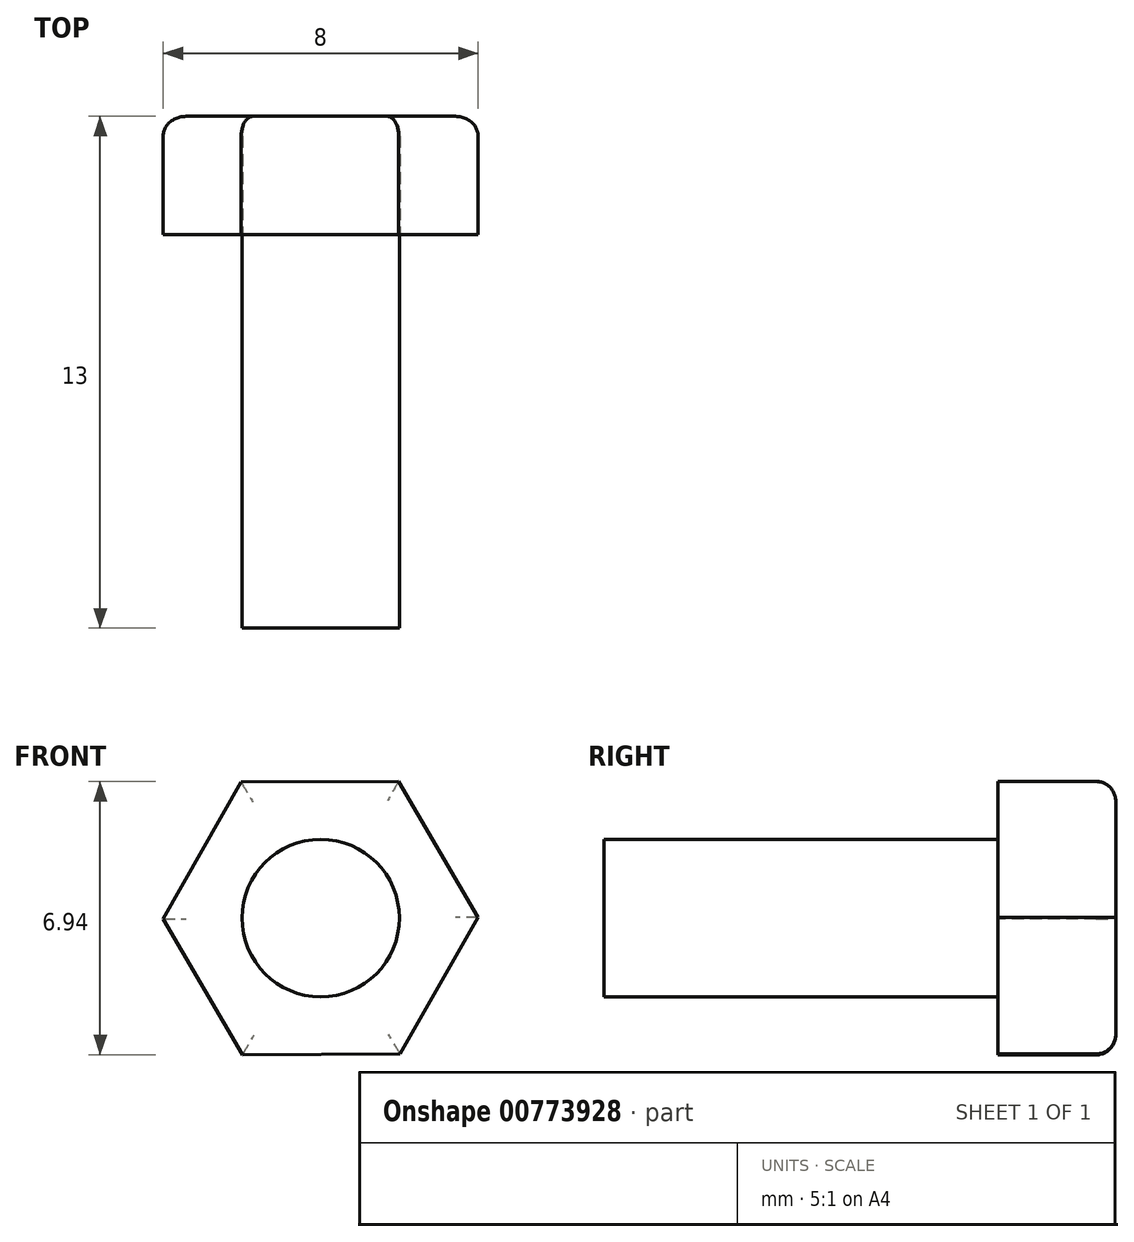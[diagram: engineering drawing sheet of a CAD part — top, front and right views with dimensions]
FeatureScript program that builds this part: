
annotation { "Feature Type Name" : "Feature", "Feature Type Description" : "" }
export const myFeature = defineFeature(function(context is Context, id is Id, definition is map)
    precondition{}
    {
        {
            var Q0;
            Q0=qCreatedBy(makeId("Front.planeOp"),FACE);
            var sketch = newSketch(context, id + "F0", { "sketchPlane" : qUnion([Q0])});
            skCircle(sketch, "E0", {"center": v(0, 0) * mm, "radius": 2 * mm});
            skSolve(sketch);
        }
        {
            var Q0;
            Q0 = qSketchRegion(id + "F0", true);
            extrude(context, id + "F1", {"entities" : qUnion([Q0]), "oppositeDirection" : true, "depth" : 10 * mm, "offsetDistance" : 25 * mm});
        }
        {
            var Q0;
            Q0=makeQuery(id+"F1.opExtrude","CAP_FACE",FACE,{"disambiguationData":[OSD([sQuery(id+"F0.wireOp",EDGE,"E0")])],"isStart":false});
            var sketch = newSketch(context, id + "F2", { "sketchPlane" : qUnion([Q0])});
            skCircle(sketch, "E1.cCircle", {"center": v(0, 0) * mm, "radius": 4 * mm, "construction": true});
            skLineSegment(sketch, "E1.0", {"start": v(2.02, 3.45) * mm, "end": v(4, -0.02) * mm});
            skLineSegment(sketch, "E1.1", {"start": v(4, -0.02) * mm, "end": v(1.98, -3.47) * mm});
            skLineSegment(sketch, "E1.2", {"start": v(1.98, -3.47) * mm, "end": v(-2.02, -3.45) * mm});
            skLineSegment(sketch, "E1.3", {"start": v(-2.02, -3.45) * mm, "end": v(-4, 0.02) * mm});
            skLineSegment(sketch, "E1.4", {"start": v(-4, 0.02) * mm, "end": v(-1.98, 3.47) * mm});
            skLineSegment(sketch, "E1.5", {"start": v(-1.98, 3.47) * mm, "end": v(2.02, 3.45) * mm});
            skSolve(sketch);
        }
        {
            var Q0;
            Q0 = qSketchRegion(id + "F2", true);
            extrude(context, id + "F3", {"entities" : qUnion([Q0]), "operationType" : NewBodyOperationType.ADD, "depth" : 3 * mm, "offsetDistance" : 25 * mm});
        }
        {
            var Q0;
            Q0=makeQuery(id+"F3.opExtrude","CAP_FACE",FACE,{"disambiguationData":[OSD([sQuery(id+"F2.wireOp",EDGE,"E1.0"),sQuery(id+"F2.wireOp",EDGE,"E1.1"),sQuery(id+"F2.wireOp",EDGE,"E1.2"),sQuery(id+"F2.wireOp",EDGE,"E1.3"),sQuery(id+"F2.wireOp",EDGE,"E1.4"),sQuery(id+"F2.wireOp",EDGE,"E1.5")])],"isStart":false});
            fillet(context, id + "F4", {"entities" : qUnion([Q0]), "radius" : 0.5 * mm, "tangentPropagation" : true, "allowEdgeOverflow" : false});
        }
    });
